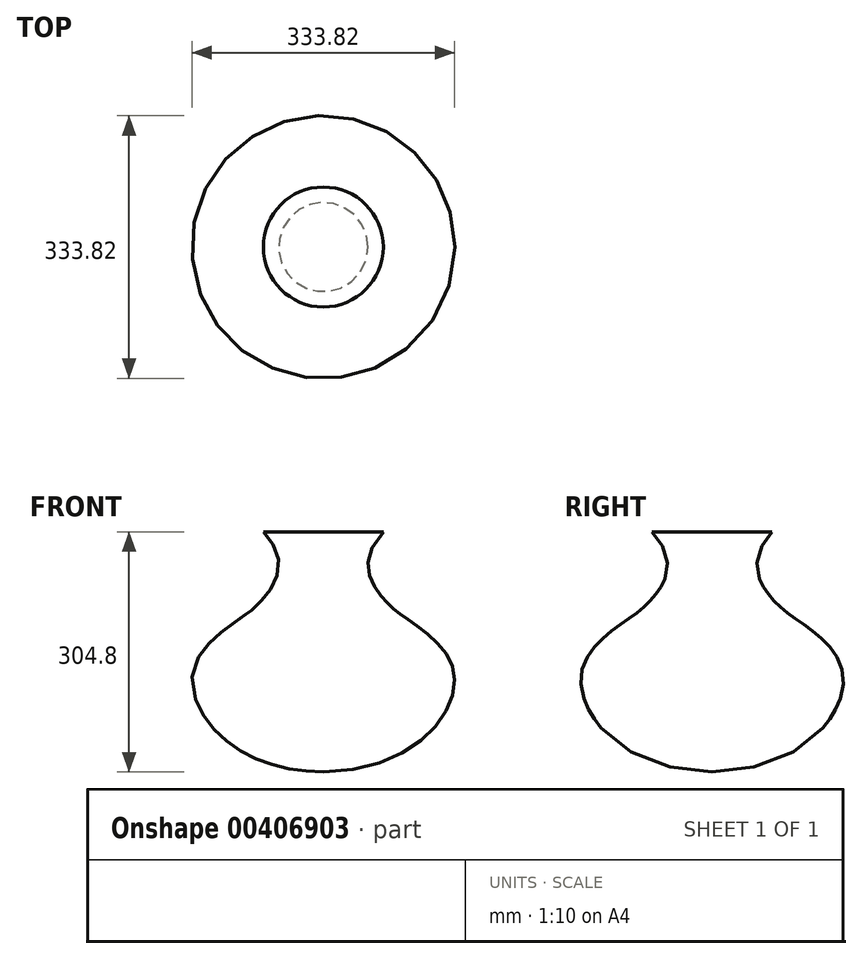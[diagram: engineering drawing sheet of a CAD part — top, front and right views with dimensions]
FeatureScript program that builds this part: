
annotation { "Feature Type Name" : "Feature", "Feature Type Description" : "" }
export const myFeature = defineFeature(function(context is Context, id is Id, definition is map)
    precondition{}
    {
        {
            var Q0;
            Q0=qCreatedBy(makeId("Front.planeOp"),FACE);
            var sketch = newSketch(context, id + "F0", { "sketchPlane" : qUnion([Q0])});
            skLineSegment(sketch, "E0", {"start": v(0, 0) * mm, "end": v(0, 304.8) * mm});
            skLineSegment(sketch, "E1", {"start": v(0, 304.8) * mm, "end": v(76.2, 304.8) * mm});
            skFitSpline(sketch, "E2", {"points": [v(0, 0) * mm, v(166.5, 122.94) * mm, v(108.85, 192.48) * mm, v(76.2, 220.14) * mm, v(76.2, 304.8) * mm], "startDerivative": vector(923.86, 0) * mm, "endDerivative": vector(455.32, 487.33) * mm});
            skSolve(sketch);
        }
        {
            var Q0;
            Q0=makeQuery(id+"F0.imprint","IMPRINT",FACE,{"disambiguationData":[TD([[makeQuery(id+"F0.imprint","IMPRINT",EDGE,{"derivedFrom":sQuery(id+"F0.wireOp",EDGE,"E0")}),-1.0]])]});
            var Q1;
            Q1=sQuery(id+"F0.wireOp",EDGE,"E0");
            revolve(context, id + "F1", {"entities" : qUnion([Q0]), "axis" : qUnion([Q1]), "revolveType" : RevolveType.FULL});
        }
    });
